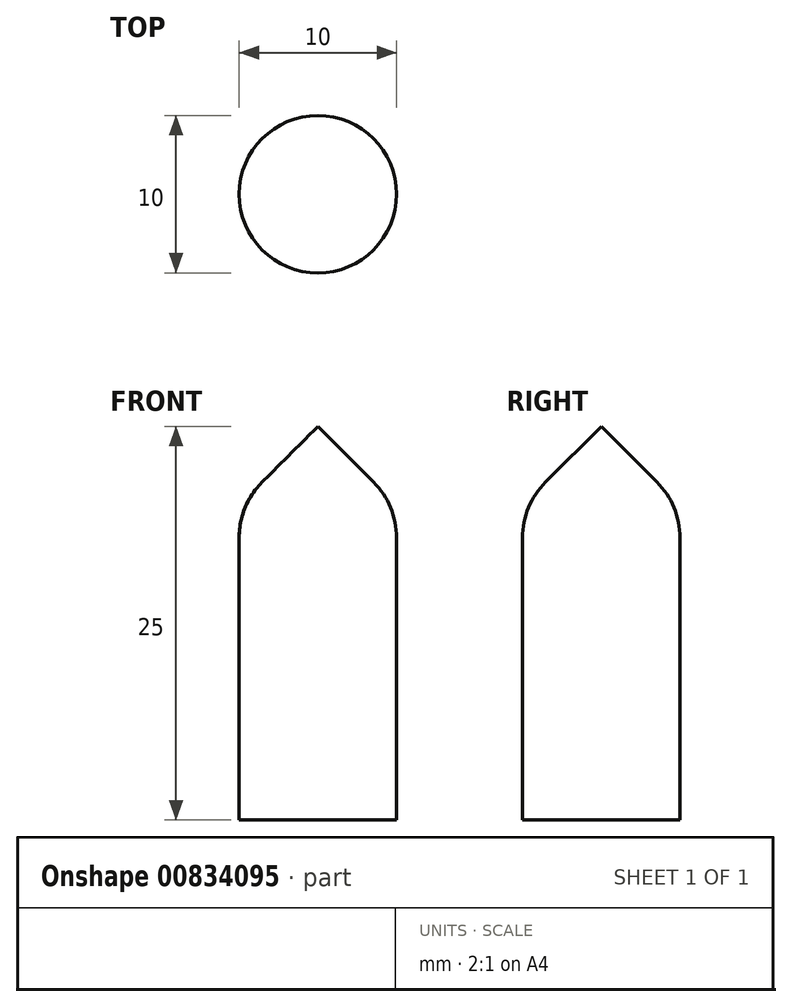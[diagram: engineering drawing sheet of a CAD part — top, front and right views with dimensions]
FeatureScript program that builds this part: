
annotation { "Feature Type Name" : "Feature", "Feature Type Description" : "" }
export const myFeature = defineFeature(function(context is Context, id is Id, definition is map)
    precondition{}
    {
        {
            var Q0;
            Q0=qCreatedBy(makeId("Top.planeOp"),FACE);
            var sketch = newSketch(context, id + "F0", { "sketchPlane" : qUnion([Q0])});
            skCircle(sketch, "E0", {"center": v(0, 0) * mm, "radius": 5 * mm});
            skSolve(sketch);
        }
        {
            var Q0;
            Q0=makeQuery(id+"F0.imprint","IMPRINT",FACE,{"disambiguationData":[TD([[makeQuery(id+"F0.imprint","IMPRINT",EDGE,{"derivedFrom":sQuery(id+"F0.wireOp",EDGE,"E0")}),1.0]])]});
            extrude(context, id + "F1", {"entities" : qUnion([Q0]), "depth" : 25 * mm, "offsetDistance" : 25 * mm});
        }
        {
            var Q0;
            Q0=makeQuery(id+"F1.opExtrude","CAP_EDGE",EDGE,{"disambiguationData":[OSD([sQuery(id+"F0.wireOp",EDGE,"E0")])],"isStart":false});
            chamfer(context, id + "F2", {"entities" : qUnion([Q0]), "width" : 5 * mm, "tangentPropagation" : true});
        }
        {
            var Q0;
            {var subQ0=sQuery(id+"F0.wireOp",EDGE,"E0");Q0=makeQuery(id+"F2.opChamfer","BLEND_EDGE",EDGE,{"blendedFrom":[makeQuery(id+"F1.opExtrude","CAP_EDGE",EDGE,{"disambiguationData":[OSD([subQ0])],"isStart":false}),makeQuery(id+"F1.opExtrude","SWEPT_FACE",FACE,{"disambiguationData":[OSD([subQ0])]})],"blendedInto":[makeQuery(id+"F1.opExtrude","SWEPT_FACE",FACE,{"disambiguationData":[OSD([subQ0])]})]});}
            fillet(context, id + "F3", {"entities" : qUnion([Q0]), "radius" : 5 * mm, "tangentPropagation" : true, "allowEdgeOverflow" : false});
        }
    });
